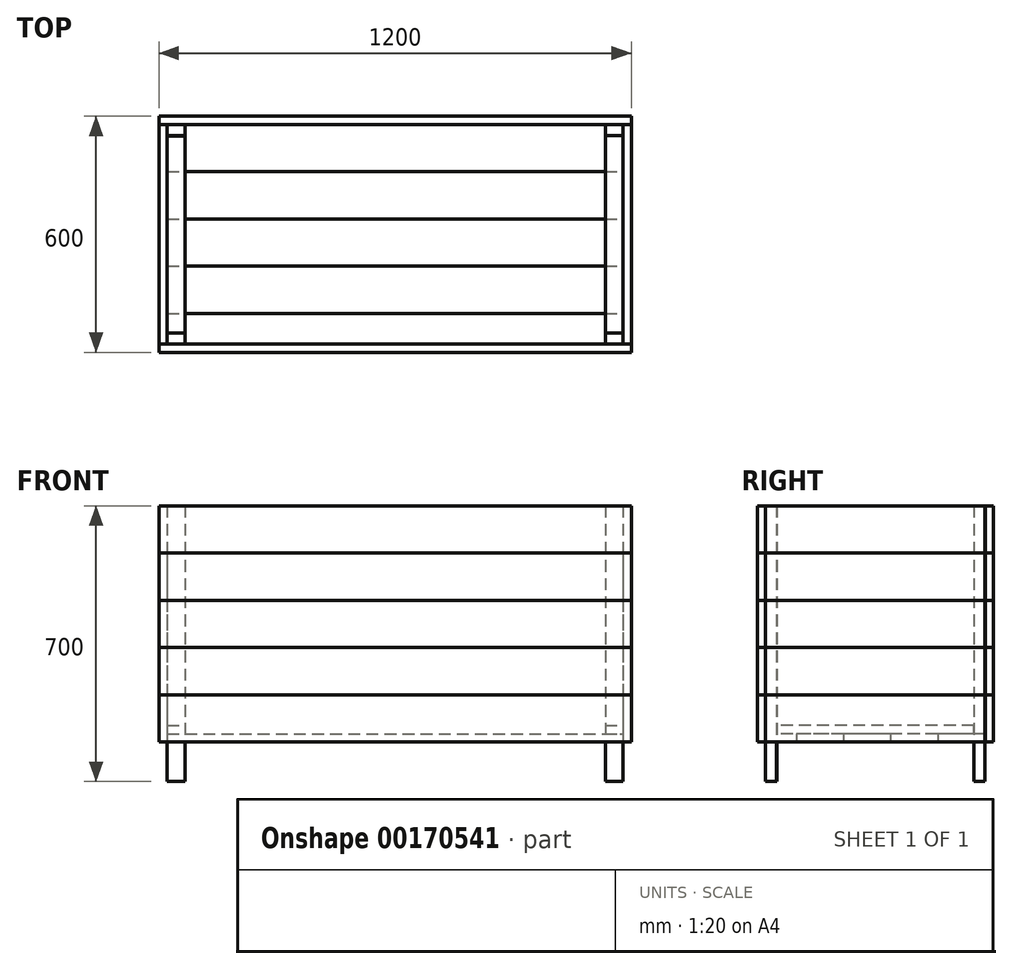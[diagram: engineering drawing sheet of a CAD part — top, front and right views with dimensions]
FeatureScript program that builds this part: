
annotation { "Feature Type Name" : "Feature", "Feature Type Description" : "" }
export const myFeature = defineFeature(function(context is Context, id is Id, definition is map)
    precondition{}
    {
        {
            var Q0;
            Q0=qCreatedBy(makeId("Top.planeOp"),FACE);
            var sketch = newSketch(context, id + "F0", { "sketchPlane" : qUnion([Q0])});
            skLineSegment(sketch, "E0.bottom", {"start": v(-600, 0) * mm, "end": v(600, 0) * mm});
            skLineSegment(sketch, "E0.top", {"start": v(-600, -21) * mm, "end": v(600, -21) * mm});
            skLineSegment(sketch, "E0.left", {"start": v(-600, 0) * mm, "end": v(-600, -21) * mm});
            skLineSegment(sketch, "E0.right", {"start": v(600, 0) * mm, "end": v(600, -21) * mm});
            skLineSegment(sketch, "E1.bottom", {"start": v(600, 579) * mm, "end": v(-600, 579) * mm});
            skLineSegment(sketch, "E1.top", {"start": v(600, 558) * mm, "end": v(-600, 558) * mm});
            skLineSegment(sketch, "E1.left", {"start": v(600, 579) * mm, "end": v(600, 558) * mm});
            skLineSegment(sketch, "E1.right", {"start": v(-600, 579) * mm, "end": v(-600, 558) * mm});
            skLineSegment(sketch, "E2.bottom", {"start": v(-600, 557.2) * mm, "end": v(-579, 557.2) * mm});
            skLineSegment(sketch, "E2.top", {"start": v(-600, 0.42) * mm, "end": v(-579, 0.42) * mm});
            skLineSegment(sketch, "E2.left", {"start": v(-600, 557.2) * mm, "end": v(-600, 0.42) * mm});
            skLineSegment(sketch, "E2.right", {"start": v(-579, 557.2) * mm, "end": v(-579, 0.42) * mm});
            skLineSegment(sketch, "E3.bottom", {"start": v(600, 557.37) * mm, "end": v(579, 557.37) * mm});
            skLineSegment(sketch, "E3.top", {"start": v(600, 0.18) * mm, "end": v(579, 0.18) * mm});
            skLineSegment(sketch, "E3.left", {"start": v(600, 557.37) * mm, "end": v(600, 0.18) * mm});
            skLineSegment(sketch, "E3.right", {"start": v(579, 557.37) * mm, "end": v(579, 0.18) * mm});
            skSolve(sketch);
        }
        {
            var Q0;
            Q0 = qSketchRegion(id + "F0", true);
            extrude(context, id + "F1", {"entities" : qUnion([Q0]), "depth" : 120 * mm});
        }
        {
            var Q0;
            Q0=makeQuery(id+"F1.opExtrude","SWEPT_BODY",BODY,{"disambiguationData":[OSD([sQuery(id+"F0.wireOp",EDGE,"E0.bottom"),sQuery(id+"F0.wireOp",EDGE,"E0.top"),sQuery(id+"F0.wireOp",EDGE,"E0.left"),sQuery(id+"F0.wireOp",EDGE,"E0.right")])]});
            transform(context, id + "F2", {"entities" : qUnion([Q0]), "transformType" : TransformType.TRANSLATION_3D, "dx" : 0 * mm, "dy" : 0 * mm, "dz" : 120 * mm, "makeCopy" : true});
        }
        {
            var Q0;
            Q0=makeQuery(id+"F2.opPattern","COPY",BODY,{"derivedFrom":makeQuery(id+"F1.opExtrude","SWEPT_BODY",BODY,{"disambiguationData":[OSD([sQuery(id+"F0.wireOp",EDGE,"E0.bottom"),sQuery(id+"F0.wireOp",EDGE,"E0.top"),sQuery(id+"F0.wireOp",EDGE,"E0.left"),sQuery(id+"F0.wireOp",EDGE,"E0.right")])]}),"instanceName":"1"});
            transform(context, id + "F3", {"entities" : qUnion([Q0]), "transformType" : TransformType.TRANSLATION_3D, "dx" : 0 * mm, "dy" : 0 * mm, "dz" : 120 * mm, "makeCopy" : true});
        }
        {
            var Q0;
            Q0=makeQuery(id+"F3.opPattern","COPY",BODY,{"derivedFrom":makeQuery(id+"F2.opPattern","COPY",BODY,{"derivedFrom":makeQuery(id+"F1.opExtrude","SWEPT_BODY",BODY,{"disambiguationData":[OSD([sQuery(id+"F0.wireOp",EDGE,"E0.bottom"),sQuery(id+"F0.wireOp",EDGE,"E0.top"),sQuery(id+"F0.wireOp",EDGE,"E0.left"),sQuery(id+"F0.wireOp",EDGE,"E0.right")])]}),"instanceName":"1"}),"instanceName":"1"});
            transform(context, id + "F4", {"entities" : qUnion([Q0]), "transformType" : TransformType.TRANSLATION_3D, "dx" : 0 * mm, "dy" : 0 * mm, "dz" : 120 * mm, "makeCopy" : true});
        }
        {
            var Q0;
            Q0=makeQuery(id+"F3.opPattern","COPY",BODY,{"derivedFrom":makeQuery(id+"F2.opPattern","COPY",BODY,{"derivedFrom":makeQuery(id+"F1.opExtrude","SWEPT_BODY",BODY,{"disambiguationData":[OSD([sQuery(id+"F0.wireOp",EDGE,"E0.bottom"),sQuery(id+"F0.wireOp",EDGE,"E0.top"),sQuery(id+"F0.wireOp",EDGE,"E0.left"),sQuery(id+"F0.wireOp",EDGE,"E0.right")])]}),"instanceName":"1"}),"instanceName":"1"});
            transform(context, id + "F5", {"entities" : qUnion([Q0]), "transformType" : TransformType.TRANSLATION_3D, "dx" : 0 * mm, "dy" : 0 * mm, "dz" : 120 * mm, "makeCopy" : true});
        }
        {
            var Q0;
            Q0=makeQuery(id+"F5.opPattern","COPY",BODY,{"derivedFrom":makeQuery(id+"F3.opPattern","COPY",BODY,{"derivedFrom":makeQuery(id+"F2.opPattern","COPY",BODY,{"derivedFrom":makeQuery(id+"F1.opExtrude","SWEPT_BODY",BODY,{"disambiguationData":[OSD([sQuery(id+"F0.wireOp",EDGE,"E0.bottom"),sQuery(id+"F0.wireOp",EDGE,"E0.top"),sQuery(id+"F0.wireOp",EDGE,"E0.left"),sQuery(id+"F0.wireOp",EDGE,"E0.right")])]}),"instanceName":"1"}),"instanceName":"1"}),"instanceName":"1"});
            deleteBodies(context, id + "F6", {"entities" : qUnion([Q0])});
        }
        {
            var Q0;
            Q0=makeQuery(id+"F4.opPattern","COPY",BODY,{"derivedFrom":makeQuery(id+"F3.opPattern","COPY",BODY,{"derivedFrom":makeQuery(id+"F2.opPattern","COPY",BODY,{"derivedFrom":makeQuery(id+"F1.opExtrude","SWEPT_BODY",BODY,{"disambiguationData":[OSD([sQuery(id+"F0.wireOp",EDGE,"E0.bottom"),sQuery(id+"F0.wireOp",EDGE,"E0.top"),sQuery(id+"F0.wireOp",EDGE,"E0.left"),sQuery(id+"F0.wireOp",EDGE,"E0.right")])]}),"instanceName":"1"}),"instanceName":"1"}),"instanceName":"1"});
            deleteBodies(context, id + "F7", {"entities" : qUnion([Q0])});
        }
        {
            var Q0;
            Q0=makeQuery(id+"F3.opPattern","COPY",BODY,{"derivedFrom":makeQuery(id+"F2.opPattern","COPY",BODY,{"derivedFrom":makeQuery(id+"F1.opExtrude","SWEPT_BODY",BODY,{"disambiguationData":[OSD([sQuery(id+"F0.wireOp",EDGE,"E0.bottom"),sQuery(id+"F0.wireOp",EDGE,"E0.top"),sQuery(id+"F0.wireOp",EDGE,"E0.left"),sQuery(id+"F0.wireOp",EDGE,"E0.right")])]}),"instanceName":"1"}),"instanceName":"1"});
            transform(context, id + "F8", {"entities" : qUnion([Q0]), "transformType" : TransformType.TRANSLATION_3D, "dx" : 0 * mm, "dy" : 0 * mm, "dz" : 120 * mm, "makeCopy" : true});
        }
        {
            var Q0;
            Q0=makeQuery(id+"F8.opPattern","COPY",BODY,{"derivedFrom":makeQuery(id+"F3.opPattern","COPY",BODY,{"derivedFrom":makeQuery(id+"F2.opPattern","COPY",BODY,{"derivedFrom":makeQuery(id+"F1.opExtrude","SWEPT_BODY",BODY,{"disambiguationData":[OSD([sQuery(id+"F0.wireOp",EDGE,"E0.bottom"),sQuery(id+"F0.wireOp",EDGE,"E0.top"),sQuery(id+"F0.wireOp",EDGE,"E0.left"),sQuery(id+"F0.wireOp",EDGE,"E0.right")])]}),"instanceName":"1"}),"instanceName":"1"}),"instanceName":"1"});
            transform(context, id + "F9", {"entities" : qUnion([Q0]), "transformType" : TransformType.TRANSLATION_3D, "dx" : 0 * mm, "dy" : 0 * mm, "dz" : 120 * mm, "makeCopy" : true});
        }
        {
            var Q0;
            Q0=makeQuery(id+"F1.opExtrude","SWEPT_BODY",BODY,{"disambiguationData":[OSD([sQuery(id+"F0.wireOp",EDGE,"E1.bottom"),sQuery(id+"F0.wireOp",EDGE,"E1.top"),sQuery(id+"F0.wireOp",EDGE,"E1.left"),sQuery(id+"F0.wireOp",EDGE,"E1.right")])]});
            transform(context, id + "F10", {"entities" : qUnion([Q0]), "transformType" : TransformType.TRANSLATION_3D, "dx" : 0 * mm, "dy" : 0 * mm, "dz" : 120 * mm, "makeCopy" : true});
        }
        {
            var Q0;
            Q0=makeQuery(id+"F10.opPattern","COPY",BODY,{"derivedFrom":makeQuery(id+"F1.opExtrude","SWEPT_BODY",BODY,{"disambiguationData":[OSD([sQuery(id+"F0.wireOp",EDGE,"E1.bottom"),sQuery(id+"F0.wireOp",EDGE,"E1.top"),sQuery(id+"F0.wireOp",EDGE,"E1.left"),sQuery(id+"F0.wireOp",EDGE,"E1.right")])]}),"instanceName":"1"});
            transform(context, id + "F11", {"entities" : qUnion([Q0]), "transformType" : TransformType.TRANSLATION_3D, "dx" : 0 * mm, "dy" : 0 * mm, "dz" : 120 * mm, "makeCopy" : true});
        }
        {
            var Q0;
            Q0=makeQuery(id+"F11.opPattern","COPY",BODY,{"derivedFrom":makeQuery(id+"F10.opPattern","COPY",BODY,{"derivedFrom":makeQuery(id+"F1.opExtrude","SWEPT_BODY",BODY,{"disambiguationData":[OSD([sQuery(id+"F0.wireOp",EDGE,"E1.bottom"),sQuery(id+"F0.wireOp",EDGE,"E1.top"),sQuery(id+"F0.wireOp",EDGE,"E1.left"),sQuery(id+"F0.wireOp",EDGE,"E1.right")])]}),"instanceName":"1"}),"instanceName":"1"});
            transform(context, id + "F12", {"entities" : qUnion([Q0]), "transformType" : TransformType.TRANSLATION_3D, "dx" : 0 * mm, "dy" : 0 * mm, "dz" : 120 * mm, "makeCopy" : true});
        }
        {
            var Q0;
            Q0=makeQuery(id+"F12.opPattern","COPY",BODY,{"derivedFrom":makeQuery(id+"F11.opPattern","COPY",BODY,{"derivedFrom":makeQuery(id+"F10.opPattern","COPY",BODY,{"derivedFrom":makeQuery(id+"F1.opExtrude","SWEPT_BODY",BODY,{"disambiguationData":[OSD([sQuery(id+"F0.wireOp",EDGE,"E1.bottom"),sQuery(id+"F0.wireOp",EDGE,"E1.top"),sQuery(id+"F0.wireOp",EDGE,"E1.left"),sQuery(id+"F0.wireOp",EDGE,"E1.right")])]}),"instanceName":"1"}),"instanceName":"1"}),"instanceName":"1"});
            transform(context, id + "F13", {"entities" : qUnion([Q0]), "transformType" : TransformType.TRANSLATION_3D, "dx" : 0 * mm, "dy" : 0 * mm, "dz" : 120 * mm, "makeCopy" : true});
        }
        {
            var Q0;
            Q0=makeQuery(id+"F1.opExtrude","SWEPT_BODY",BODY,{"disambiguationData":[OSD([sQuery(id+"F0.wireOp",EDGE,"E2.bottom"),sQuery(id+"F0.wireOp",EDGE,"E2.top"),sQuery(id+"F0.wireOp",EDGE,"E2.left"),sQuery(id+"F0.wireOp",EDGE,"E2.right")])]});
            transform(context, id + "F14", {"entities" : qUnion([Q0]), "transformType" : TransformType.TRANSLATION_3D, "dx" : 0 * mm, "dy" : 0 * mm, "dz" : 120 * mm, "makeCopy" : true});
        }
        {
            var Q0;
            Q0=makeQuery(id+"F14.opPattern","COPY",BODY,{"derivedFrom":makeQuery(id+"F1.opExtrude","SWEPT_BODY",BODY,{"disambiguationData":[OSD([sQuery(id+"F0.wireOp",EDGE,"E2.bottom"),sQuery(id+"F0.wireOp",EDGE,"E2.top"),sQuery(id+"F0.wireOp",EDGE,"E2.left"),sQuery(id+"F0.wireOp",EDGE,"E2.right")])]}),"instanceName":"1"});
            transform(context, id + "F15", {"entities" : qUnion([Q0]), "transformType" : TransformType.TRANSLATION_3D, "dx" : 0 * mm, "dy" : 0 * mm, "dz" : 120 * mm, "makeCopy" : true});
        }
        {
            var Q0;
            Q0=makeQuery(id+"F15.opPattern","COPY",BODY,{"derivedFrom":makeQuery(id+"F14.opPattern","COPY",BODY,{"derivedFrom":makeQuery(id+"F1.opExtrude","SWEPT_BODY",BODY,{"disambiguationData":[OSD([sQuery(id+"F0.wireOp",EDGE,"E2.bottom"),sQuery(id+"F0.wireOp",EDGE,"E2.top"),sQuery(id+"F0.wireOp",EDGE,"E2.left"),sQuery(id+"F0.wireOp",EDGE,"E2.right")])]}),"instanceName":"1"}),"instanceName":"1"});
            transform(context, id + "F16", {"entities" : qUnion([Q0]), "transformType" : TransformType.TRANSLATION_3D, "dx" : 0 * mm, "dy" : 0 * mm, "dz" : 120 * mm, "makeCopy" : true});
        }
        {
            var Q0;
            Q0=makeQuery(id+"F16.opPattern","COPY",BODY,{"derivedFrom":makeQuery(id+"F15.opPattern","COPY",BODY,{"derivedFrom":makeQuery(id+"F14.opPattern","COPY",BODY,{"derivedFrom":makeQuery(id+"F1.opExtrude","SWEPT_BODY",BODY,{"disambiguationData":[OSD([sQuery(id+"F0.wireOp",EDGE,"E2.bottom"),sQuery(id+"F0.wireOp",EDGE,"E2.top"),sQuery(id+"F0.wireOp",EDGE,"E2.left"),sQuery(id+"F0.wireOp",EDGE,"E2.right")])]}),"instanceName":"1"}),"instanceName":"1"}),"instanceName":"1"});
            transform(context, id + "F17", {"entities" : qUnion([Q0]), "transformType" : TransformType.TRANSLATION_3D, "dx" : 0 * mm, "dy" : 0 * mm, "dz" : 120 * mm, "makeCopy" : true});
        }
        {
            var Q0;
            Q0=makeQuery(id+"F1.opExtrude","SWEPT_BODY",BODY,{"disambiguationData":[OSD([sQuery(id+"F0.wireOp",EDGE,"E3.bottom"),sQuery(id+"F0.wireOp",EDGE,"E3.top"),sQuery(id+"F0.wireOp",EDGE,"E3.left"),sQuery(id+"F0.wireOp",EDGE,"E3.right")])]});
            transform(context, id + "F18", {"entities" : qUnion([Q0]), "transformType" : TransformType.TRANSLATION_3D, "dx" : 0 * mm, "dy" : 0 * mm, "dz" : 120 * mm, "makeCopy" : true});
        }
        {
            var Q0;
            Q0=makeQuery(id+"F18.opPattern","COPY",BODY,{"derivedFrom":makeQuery(id+"F1.opExtrude","SWEPT_BODY",BODY,{"disambiguationData":[OSD([sQuery(id+"F0.wireOp",EDGE,"E3.bottom"),sQuery(id+"F0.wireOp",EDGE,"E3.top"),sQuery(id+"F0.wireOp",EDGE,"E3.left"),sQuery(id+"F0.wireOp",EDGE,"E3.right")])]}),"instanceName":"1"});
            transform(context, id + "F19", {"entities" : qUnion([Q0]), "transformType" : TransformType.TRANSLATION_3D, "dx" : 0 * mm, "dy" : 0 * mm, "dz" : 120 * mm, "makeCopy" : true});
        }
        {
            var Q0;
            Q0=makeQuery(id+"F19.opPattern","COPY",BODY,{"derivedFrom":makeQuery(id+"F18.opPattern","COPY",BODY,{"derivedFrom":makeQuery(id+"F1.opExtrude","SWEPT_BODY",BODY,{"disambiguationData":[OSD([sQuery(id+"F0.wireOp",EDGE,"E3.bottom"),sQuery(id+"F0.wireOp",EDGE,"E3.top"),sQuery(id+"F0.wireOp",EDGE,"E3.left"),sQuery(id+"F0.wireOp",EDGE,"E3.right")])]}),"instanceName":"1"}),"instanceName":"1"});
            transform(context, id + "F20", {"entities" : qUnion([Q0]), "transformType" : TransformType.TRANSLATION_3D, "dx" : 0 * mm, "dy" : 0 * mm, "dz" : 120 * mm, "makeCopy" : true});
        }
        {
            var Q0;
            Q0=makeQuery(id+"F20.opPattern","COPY",BODY,{"derivedFrom":makeQuery(id+"F19.opPattern","COPY",BODY,{"derivedFrom":makeQuery(id+"F18.opPattern","COPY",BODY,{"derivedFrom":makeQuery(id+"F1.opExtrude","SWEPT_BODY",BODY,{"disambiguationData":[OSD([sQuery(id+"F0.wireOp",EDGE,"E3.bottom"),sQuery(id+"F0.wireOp",EDGE,"E3.top"),sQuery(id+"F0.wireOp",EDGE,"E3.left"),sQuery(id+"F0.wireOp",EDGE,"E3.right")])]}),"instanceName":"1"}),"instanceName":"1"}),"instanceName":"1"});
            transform(context, id + "F21", {"entities" : qUnion([Q0]), "transformType" : TransformType.TRANSLATION_3D, "dx" : 0 * mm, "dy" : 0 * mm, "dz" : 120 * mm, "makeCopy" : true});
        }
        {
            var Q0;
            Q0=qCreatedBy(makeId("Top.planeOp"),FACE);
            var sketch = newSketch(context, id + "F22", { "sketchPlane" : qUnion([Q0])});
            skLineSegment(sketch, "E4.bottom", {"start": v(-579, 557.2) * mm, "end": v(-534, 557.2) * mm});
            skLineSegment(sketch, "E4.top", {"start": v(-579, 529.2) * mm, "end": v(-534, 529.2) * mm});
            skLineSegment(sketch, "E4.left", {"start": v(-579, 557.2) * mm, "end": v(-579, 529.2) * mm});
            skLineSegment(sketch, "E4.right", {"start": v(-534, 557.2) * mm, "end": v(-534, 529.2) * mm});
            skLineSegment(sketch, "E5.bottom", {"start": v(534, 557.37) * mm, "end": v(579, 557.37) * mm});
            skLineSegment(sketch, "E5.top", {"start": v(534, 529.37) * mm, "end": v(579, 529.37) * mm});
            skLineSegment(sketch, "E5.left", {"start": v(534, 557.37) * mm, "end": v(534, 529.37) * mm});
            skLineSegment(sketch, "E5.right", {"start": v(579, 557.37) * mm, "end": v(579, 529.37) * mm});
            skLineSegment(sketch, "E6.bottom", {"start": v(-579, 28.42) * mm, "end": v(-534, 28.42) * mm});
            skLineSegment(sketch, "E6.top", {"start": v(-579, 0.42) * mm, "end": v(-534, 0.42) * mm});
            skLineSegment(sketch, "E6.left", {"start": v(-579, 28.42) * mm, "end": v(-579, 0.42) * mm});
            skLineSegment(sketch, "E6.right", {"start": v(-534, 28.42) * mm, "end": v(-534, 0.42) * mm});
            skLineSegment(sketch, "E7.bottom", {"start": v(534, 28.18) * mm, "end": v(579, 28.18) * mm});
            skLineSegment(sketch, "E7.top", {"start": v(534, 0.18) * mm, "end": v(579, 0.18) * mm});
            skLineSegment(sketch, "E7.left", {"start": v(534, 28.18) * mm, "end": v(534, 0.18) * mm});
            skLineSegment(sketch, "E7.right", {"start": v(579, 28.18) * mm, "end": v(579, 0.18) * mm});
            skSolve(sketch);
        }
        {
            var Q0;
            Q0 = qSketchRegion(id + "F22", true);
            extrude(context, id + "F23", {"entities" : qUnion([Q0]), "depth" : 600 * mm});
        }
        {
            var Q0;
            Q0 = qSketchRegion(id + "F22", true);
            extrude(context, id + "F24", {"entities" : qUnion([Q0]), "oppositeDirection" : true, "depth" : 100 * mm});
        }
        {
            var Q0;
            Q0=qCreatedBy(makeId("Top.planeOp"),FACE);
            var sketch = newSketch(context, id + "F25", { "sketchPlane" : qUnion([Q0])});
            skLineSegment(sketch, "E8.bottom", {"start": v(-578.69, 528.74) * mm, "end": v(-534.03, 528.74) * mm});
            skLineSegment(sketch, "E8.top", {"start": v(-578.69, 28.56) * mm, "end": v(-534.03, 28.56) * mm});
            skLineSegment(sketch, "E8.left", {"start": v(-578.69, 528.74) * mm, "end": v(-578.69, 28.56) * mm});
            skLineSegment(sketch, "E8.right", {"start": v(-534.03, 528.74) * mm, "end": v(-534.03, 28.56) * mm});
            skLineSegment(sketch, "E9.bottom", {"start": v(533.96, 529.09) * mm, "end": v(578.85, 529.09) * mm});
            skLineSegment(sketch, "E9.top", {"start": v(533.96, 28.16) * mm, "end": v(578.85, 28.16) * mm});
            skLineSegment(sketch, "E9.left", {"start": v(533.96, 529.09) * mm, "end": v(533.96, 28.16) * mm});
            skLineSegment(sketch, "E9.right", {"start": v(578.85, 529.09) * mm, "end": v(578.85, 28.16) * mm});
            skSolve(sketch);
        }
        {
            var Q0;
            Q0 = qSketchRegion(id + "F25", true);
            extrude(context, id + "F26", {"entities" : qUnion([Q0]), "depth" : 42 * mm, "hasSecondDirection" : true, "secondDirectionOppositeDirection" : false, "secondDirectionDepth" : 21 * mm});
        }
        {
            var Q0;
            Q0=qCreatedBy(makeId("Top.planeOp"),FACE);
            var sketch = newSketch(context, id + "F27", { "sketchPlane" : qUnion([Q0])});
            skLineSegment(sketch, "E10.bottom", {"start": v(-579, 558) * mm, "end": v(579, 558) * mm});
            skLineSegment(sketch, "E10.top", {"start": v(-579, 438) * mm, "end": v(579, 438) * mm});
            skLineSegment(sketch, "E10.left", {"start": v(-579, 558) * mm, "end": v(-579, 438) * mm});
            skLineSegment(sketch, "E10.right", {"start": v(579, 558) * mm, "end": v(579, 438) * mm});
            skSolve(sketch);
        }
        {
            var Q0;
            Q0=makeQuery(id+"F27.imprint","IMPRINT",FACE,{"disambiguationData":[TD([[makeQuery(id+"F27.imprint","IMPRINT",EDGE,{"derivedFrom":sQuery(id+"F27.wireOp",EDGE,"E10.bottom")}),-1.0]])]});
            extrude(context, id + "F28", {"entities" : qUnion([Q0]), "depth" : 21 * mm});
        }
        {
            var Q0;
            Q0=makeQuery(id+"F28.opExtrude","SWEPT_BODY",BODY,{"disambiguationData":[OSD([sQuery(id+"F27.wireOp",EDGE,"E10.bottom"),sQuery(id+"F27.wireOp",EDGE,"E10.top"),sQuery(id+"F27.wireOp",EDGE,"E10.left"),sQuery(id+"F27.wireOp",EDGE,"E10.right")])]});
            transform(context, id + "F29", {"entities" : qUnion([Q0]), "transformType" : TransformType.TRANSLATION_3D, "dx" : 0 * mm, "dy" : -120 * mm, "dz" : 0 * mm, "makeCopy" : true});
        }
        {
            var Q0;
            Q0=makeQuery(id+"F29.opPattern","COPY",BODY,{"derivedFrom":makeQuery(id+"F28.opExtrude","SWEPT_BODY",BODY,{"disambiguationData":[OSD([sQuery(id+"F27.wireOp",EDGE,"E10.bottom"),sQuery(id+"F27.wireOp",EDGE,"E10.top"),sQuery(id+"F27.wireOp",EDGE,"E10.left"),sQuery(id+"F27.wireOp",EDGE,"E10.right")])]}),"instanceName":"1"});
            transform(context, id + "F30", {"entities" : qUnion([Q0]), "transformType" : TransformType.TRANSLATION_3D, "dx" : 0 * mm, "dy" : -120 * mm, "dz" : 0 * mm, "makeCopy" : true});
        }
        {
            var Q0;
            Q0=makeQuery(id+"F30.opPattern","COPY",BODY,{"derivedFrom":makeQuery(id+"F29.opPattern","COPY",BODY,{"derivedFrom":makeQuery(id+"F28.opExtrude","SWEPT_BODY",BODY,{"disambiguationData":[OSD([sQuery(id+"F27.wireOp",EDGE,"E10.bottom"),sQuery(id+"F27.wireOp",EDGE,"E10.top"),sQuery(id+"F27.wireOp",EDGE,"E10.left"),sQuery(id+"F27.wireOp",EDGE,"E10.right")])]}),"instanceName":"1"}),"instanceName":"1"});
            transform(context, id + "F31", {"entities" : qUnion([Q0]), "transformType" : TransformType.TRANSLATION_3D, "dx" : 0 * mm, "dy" : -120 * mm, "dz" : 0 * mm, "makeCopy" : true});
        }
    });
